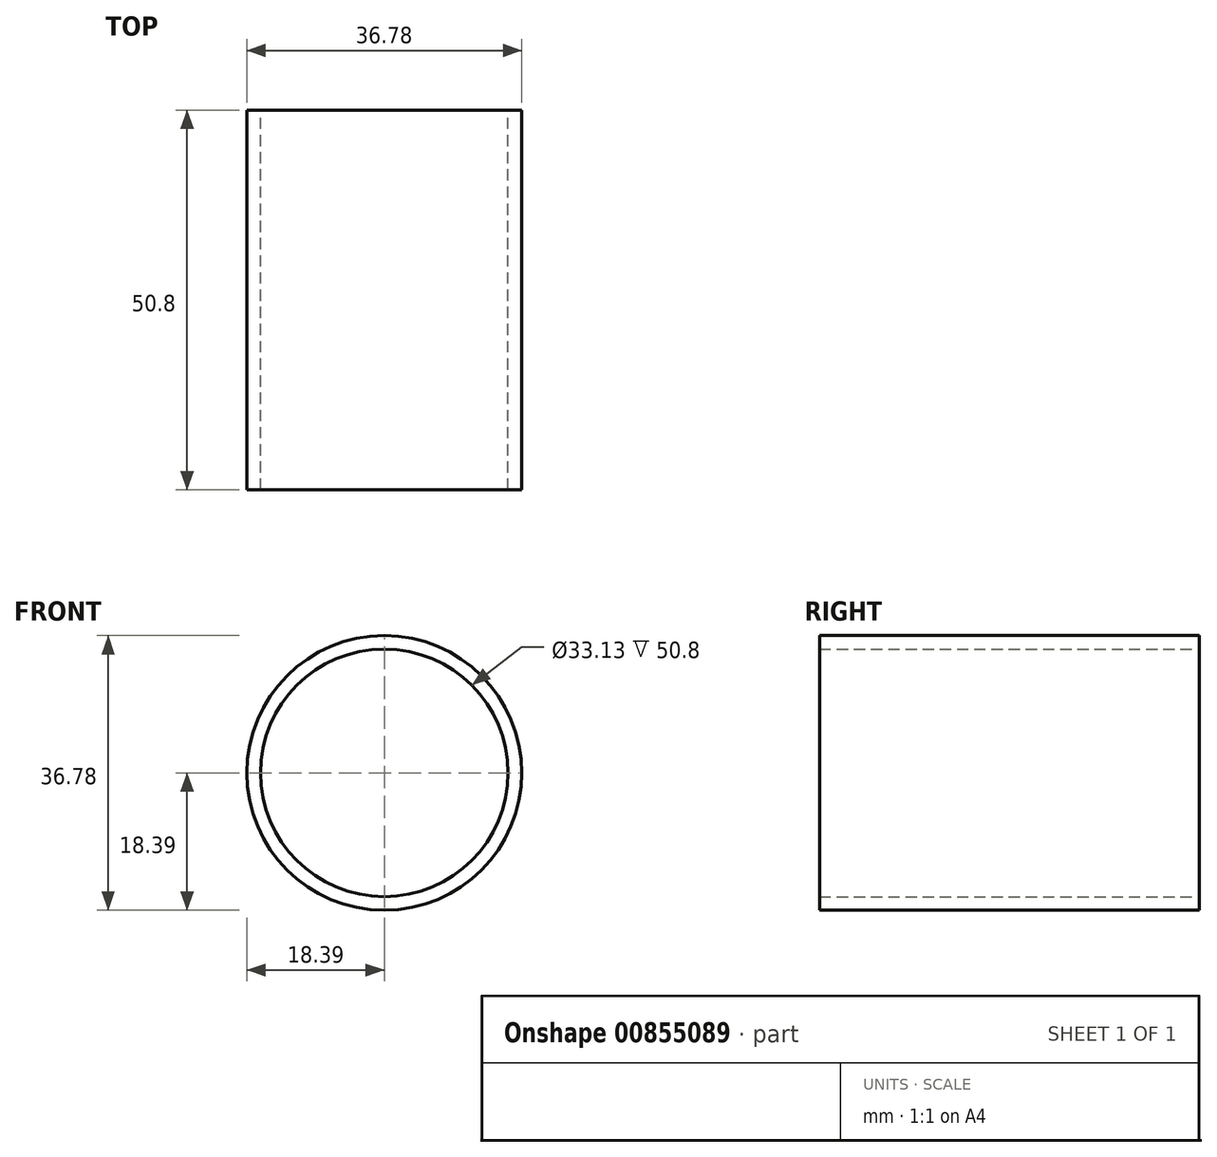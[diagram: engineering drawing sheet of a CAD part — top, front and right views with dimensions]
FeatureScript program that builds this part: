
annotation { "Feature Type Name" : "Feature", "Feature Type Description" : "" }
export const myFeature = defineFeature(function(context is Context, id is Id, definition is map)
    precondition{}
    {
        {
            var Q0;
            Q0=qCreatedBy(makeId("Front.planeOp"),FACE);
            var sketch = newSketch(context, id + "F0", { "sketchPlane" : qUnion([Q0])});
            skCircle(sketch, "E0", {"center": v(0, 0) * mm, "radius": 18.39 * mm});
            skCircle(sketch, "E1", {"center": v(0, 0) * mm, "radius": 16.56 * mm});
            skSolve(sketch);
        }
        {
            var Q0;
            Q0=makeQuery(id+"F0.imprint","IMPRINT",FACE,{"disambiguationData":[TD([[makeQuery(id+"F0.imprint","IMPRINT",EDGE,{"derivedFrom":sQuery(id+"F0.wireOp",EDGE,"E0")}),1.0]])]});
            extrude(context, id + "F1", {"entities" : qUnion([Q0]), "depth" : 50.8 * mm, "offsetDistance" : 25.4 * mm});
        }
    });
